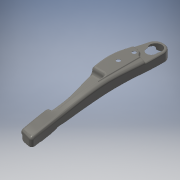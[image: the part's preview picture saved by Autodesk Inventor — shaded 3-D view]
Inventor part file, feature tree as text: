
AUTODESK INVENTOR PART (.ipt)
format: ipt  version: 2019 (Build 230136000, 136)  size: 1,342,464 bytes
history: native  units: mm
features: fillet x15, sketch x10, extrude x8, reference x8, plane x2, projected_geometry x2, revolve x1, shell x1, hole x1
ambient origin geometry x8: Origin, YZ Plane, XZ Plane, XY Plane, X Axis, Y Axis, Z Axis, Center Point
bodies: Solid1 (feature_tree)
feature tree (48):
  plane  "Work Plane2"
  extrude  "Extrusion1"  Depth=35.0mm
  fillet  "Fillet1"  Radius=4.973861mm
  plane  "Work Plane3"
  extrude  "Extrusion2"  Depth=82.311372mm TaperAngle=0.0deg
  extrude  "Extrusion3"  [1 undecoded]
  fillet  "Fillet2"  [1 undecoded]
  fillet  "Fillet3"  Radius=10.0mm
  fillet  "Fillet4"  Radius=37.0mm
  fillet  "Fillet5"  [1 undecoded]
  fillet  "Fillet6"  Radius=14.275427mm
  extrude  "Extrusion4"  Depth=1.850049mm
  fillet  "Fillet7"  Radius=211.5mm
  fillet  "Fillet10"  Radius=215.75mm
  fillet  "Fillet11"  [1 undecoded]
  fillet  "Fillet13"  Radius=7.504916mm
  fillet  "Fillet14"  Radius=419.0mm
  extrude  "Extrusion5"  Depth=12.0mm
  revolve  "Revolution1"  [1 undecoded]
  fillet  "Fillet15"  Radius=10.0mm
  shell  "Shell1"  Thickness=12.0mm
  extrude  "Extrusion6"  Depth=68.0mm
  extrude  "Extrusion7"  Depth=7.2mm
  fillet  "Fillet16"  Radius=7.5mm
  fillet  "Fillet17"  Radius=63.24061mm
  fillet  "Fillet18"  Radius=7.2mm
  extrude  "Extrusion8"  Depth=5.0mm
  hole  "Hole1"  [1 undecoded]
  sketch  "Sketch2"  dims[d0=35.0mm d1=35.0mm d2=4.973861mm]
  sketch  "Sketch4"  dims[d4=542.0mm d5=82.311372mm d6=0.0mm]
  projected_geometry  "Projected Loop1"
  sketch  "Sketch5"  dims[d7=11.0mm d8=-78.0mm d9=60.0deg d10=10.0mm d11=37.0mm d12=15.0deg d13=14.275427mm]
  sketch  "Sketch6"  dims[d14=82.311372mm d15=0.0mm d16=1.850049mm d17=211.5mm d18=215.75mm d19=75.0deg d20=7.504916mm d21=419.0mm]
  sketch  "Sketch7"  dims[d22=75.0mm d23=0.0mm d24=12.0mm]
  sketch  "Sketch9"  dims[d25=12.0mm d26=12.0mm d27=10.0mm d28=12.0mm]
  sketch  "Sketch10"  dims[d29=5.0mm d30=68.0mm]
  reference  "Reference24"
  reference  "Reference25"
  reference  "Reference26"
  projected_geometry  "Projected Loop2"
  sketch  "Sketch11"  dims[d31=55.0mm d32=45.0mm d34=7.5mm d35=63.24061mm d36=7.2mm d37=0.0mm]
  sketch  "Sketch12"  dims[d38=12.0mm d41=5.0mm]
  reference  "Reference27"
  reference  "Reference28"
  reference  "Reference29"
  reference  "Reference30"
  reference  "Reference31"
  sketch  "Sketch13"  dims[d42=11.0mm d44=4.0mm d45=4.0mm d46=1.0mm d47=6.0mm d48=8.5mm d49=250.0mm d50=0.0mm d52=3.0mm d53=90.0deg d54=90.0deg d55=90.0deg d56=2.0mm d57=250.0mm d58=0.0mm d59=27.136809mm d60=71.609537mm d61=115.663294mm d62=152.538019mm d63=212.911214mm d64=224.447904mm d65=460.752264mm d66=471.82624mm d67=537.377034mm d68=561.700492mm d69=26.558716mm d70=23.861548mm d71=14.571299mm d72=33.601324mm d73=35.798618mm d74=55.624607mm d75=61.697432mm d76=76.879496mm d77=55.624607mm d78=86.167346mm d79=5.0mm d80=10.0mm d81=8.0mm d82=60.0mm d83=0.0mm d84=10.0mm d85=5.0mm d86=5.0mm d87=49.0mm d88=41.0mm d89=20.0mm d90=24.5mm d91=19.0mm d92=10.0mm d93=10.0mm d94=60.0mm d95=0.0mm d96=64.809461mm d97=63.5mm d98=73.122637mm d99=18.683911mm d100=132.620712mm d101=16.0mm d102=6.0mm d103=4.0mm d104=2.0mm d105=90.0deg d106=8.0mm d107=20.594885mm d110=14.018111mm d111=13.730888mm]
note: 6 required parameter values undecoded (feature->parameter linkage not recoverable at this tier; creation-order binding heuristic only, values carry confidence <= 0.55)